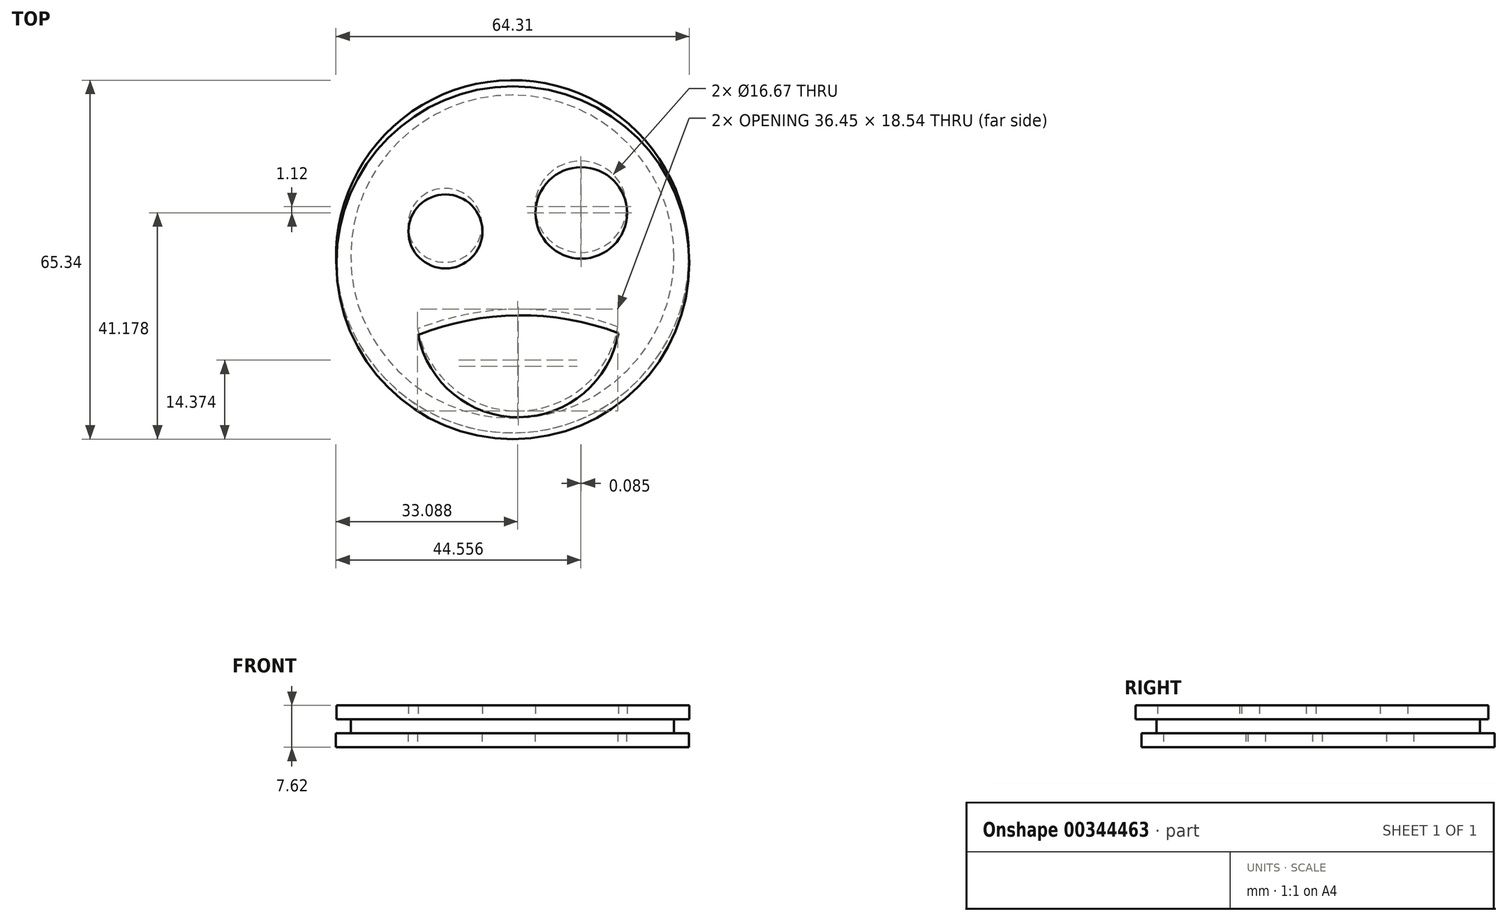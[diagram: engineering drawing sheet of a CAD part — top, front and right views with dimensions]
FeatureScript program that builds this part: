
annotation { "Feature Type Name" : "Feature", "Feature Type Description" : "" }
export const myFeature = defineFeature(function(context is Context, id is Id, definition is map)
    precondition{}
    {
        {
            var Q0;
            Q0=qCreatedBy(makeId("Top.planeOp"),FACE);
            var sketch = newSketch(context, id + "F0", { "sketchPlane" : qUnion([Q0])});
            skCircle(sketch, "E0", {"center": v(0, 0) * mm, "radius": 32.11 * mm});
            skCircle(sketch, "E1", {"center": v(12.45, 9.07) * mm, "radius": 8.33 * mm});
            skCircle(sketch, "E2", {"center": v(-12.27, 5.69) * mm, "radius": 6.73 * mm});
            skArc(sketch, "E3", {"start": v(-17.25, -13.16) * mm, "mid": v(1.13, -28.12) * mm, "end": v(19.2, -12.8) * mm});
            skArc(sketch, "E4", {"start": v(19.2, -12.8) * mm, "mid": v(0.94, -9.59) * mm, "end": v(-17.25, -13.16) * mm});
            skSolve(sketch);
        }
        {
            var Q0;
            Q0=makeQuery(id+"F0.imprint","IMPRINT",FACE,{"disambiguationData":[TD([[makeQuery(id+"F0.imprint","IMPRINT",EDGE,{"derivedFrom":sQuery(id+"F0.wireOp",EDGE,"E0")}),1.0]])]});
            extrude(context, id + "F1", {"entities" : qUnion([Q0]), "depth" : 2.54 * mm});
        }
        {
            var Q0;
            Q0=makeQuery(id+"F1.opExtrude","CAP_FACE",FACE,{"disambiguationData":[OSD([sQuery(id+"F0.wireOp",EDGE,"E0"),sQuery(id+"F0.wireOp",EDGE,"E1"),sQuery(id+"F0.wireOp",EDGE,"E2"),sQuery(id+"F0.wireOp",EDGE,"E3"),sQuery(id+"F0.wireOp",EDGE,"E4")])],"isStart":false});
            var sketch = newSketch(context, id + "F2", { "sketchPlane" : qUnion([Q0])});
            skCircle(sketch, "E5", {"center": v(0, 0) * mm, "radius": 29.42 * mm});
            skSolve(sketch);
        }
        {
            var Q0;
            Q0 = qSketchRegion(id + "F2", true);
            extrude(context, id + "F3", {"entities" : qUnion([Q0]), "depth" : 2.54 * mm});
        }
        {
            var Q0;
            Q0=makeQuery(id+"F3.opExtrude","CAP_FACE",FACE,{"disambiguationData":[OSD([sQuery(id+"F2.wireOp",EDGE,"E5")])],"isStart":false});
            var sketch = newSketch(context, id + "F4", { "sketchPlane" : qUnion([Q0])});
            skCircle(sketch, "E6", {"center": v(0.09, -1.12) * mm, "radius": 32.11 * mm});
            skCircle(sketch, "E7", {"center": v(12.53, 7.95) * mm, "radius": 8.33 * mm});
            skCircle(sketch, "E8", {"center": v(-12.18, 4.57) * mm, "radius": 6.73 * mm});
            skArc(sketch, "E9", {"start": v(-17.16, -14.28) * mm, "mid": v(1.21, -29.24) * mm, "end": v(19.29, -13.92) * mm});
            skArc(sketch, "E10", {"start": v(19.29, -13.92) * mm, "mid": v(1.03, -10.7) * mm, "end": v(-17.16, -14.28) * mm});
            skSolve(sketch);
        }
        {
            var Q0;
            Q0 = qSketchRegion(id + "F4", true);
            extrude(context, id + "F5", {"entities" : qUnion([Q0]), "depth" : 2.54 * mm});
        }
    });
